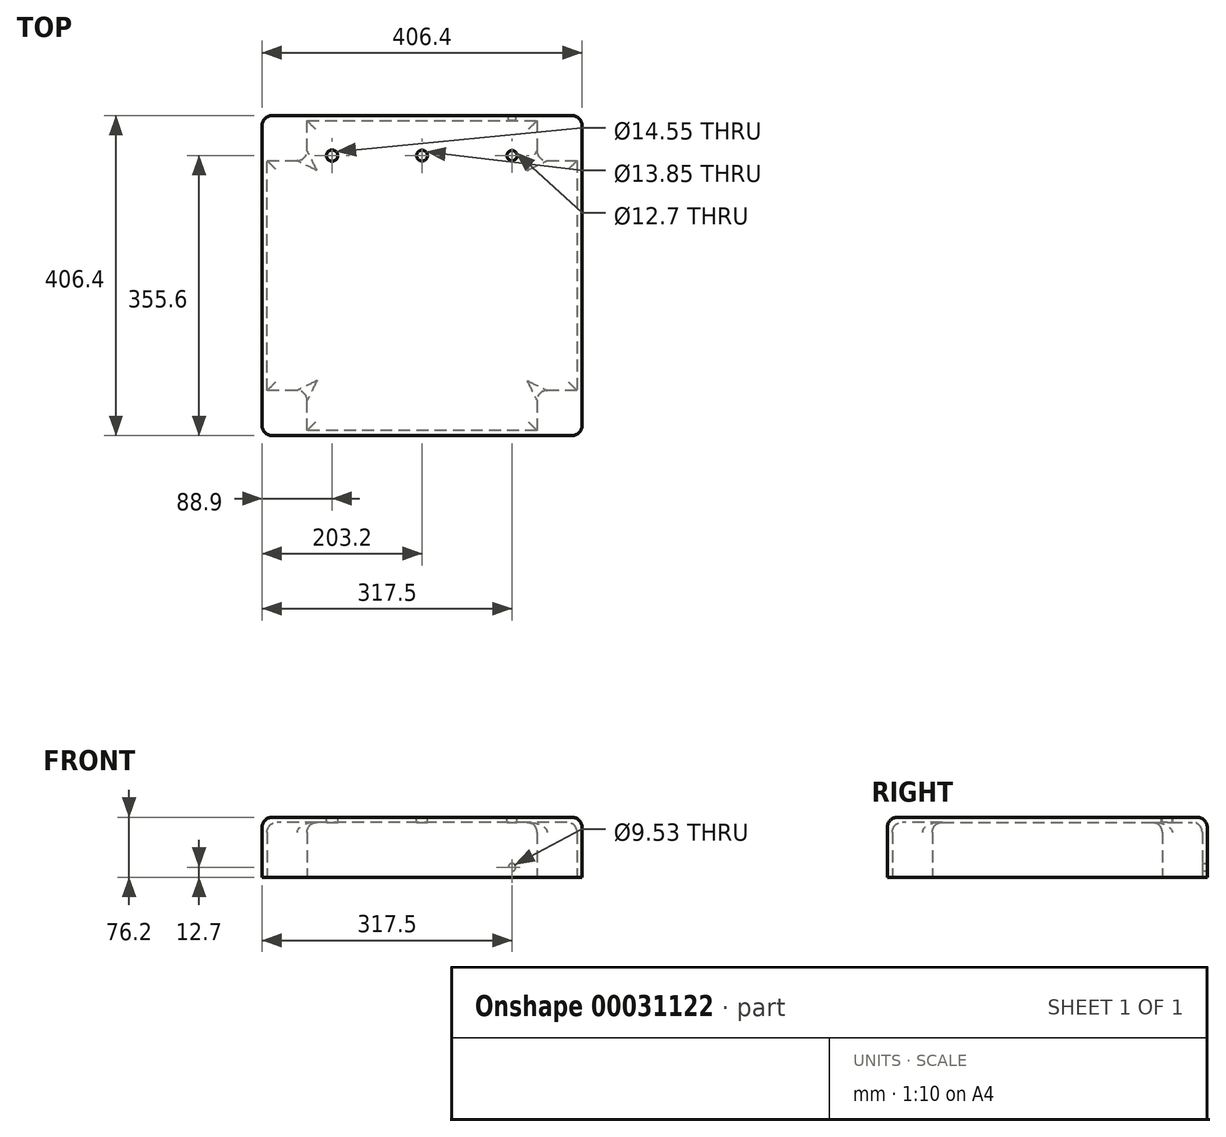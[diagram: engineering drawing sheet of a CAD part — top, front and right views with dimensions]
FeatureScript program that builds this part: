
annotation { "Feature Type Name" : "Feature", "Feature Type Description" : "" }
export const myFeature = defineFeature(function(context is Context, id is Id, definition is map)
    precondition{}
    {
        {
            var Q0;
            Q0=qCreatedBy(makeId("Top.planeOp"),FACE);
            var sketch = newSketch(context, id + "F0", { "sketchPlane" : qUnion([Q0])});
            skLineSegment(sketch, "E0.bottom", {"start": v(-203.2, 203.2) * mm, "end": v(203.2, 203.2) * mm});
            skLineSegment(sketch, "E0.top", {"start": v(-203.2, -203.2) * mm, "end": v(203.2, -203.2) * mm});
            skLineSegment(sketch, "E0.left", {"start": v(-203.2, 203.2) * mm, "end": v(-203.2, -203.2) * mm});
            skLineSegment(sketch, "E0.right", {"start": v(203.2, 203.2) * mm, "end": v(203.2, -203.2) * mm});
            skSolve(sketch);
        }
        {
            var Q0;
            Q0=makeQuery(id+"F0.imprint","IMPRINT",FACE,{"disambiguationData":[TD([[makeQuery(id+"F0.imprint","IMPRINT",EDGE,{"derivedFrom":sQuery(id+"F0.wireOp",EDGE,"E0.bottom")}),-1.0]])]});
            extrude(context, id + "F1", {"entities" : qUnion([Q0]), "depth" : 76.2 * mm});
        }
        {
            var Q0;
            Q0=makeQuery(id+"F1.opExtrude","SWEPT_EDGE",EDGE,{"disambiguationData":[OSD([sQuery(id+"F0.wireOp",EDGE,"E0.top"),sQuery(id+"F0.wireOp",EDGE,"E0.right")])]});
            var Q1;
            Q1=makeQuery(id+"F1.opExtrude","SWEPT_EDGE",EDGE,{"disambiguationData":[OSD([sQuery(id+"F0.wireOp",EDGE,"E0.bottom"),sQuery(id+"F0.wireOp",EDGE,"E0.right")])]});
            var Q2;
            Q2=makeQuery(id+"F1.opExtrude","SWEPT_EDGE",EDGE,{"disambiguationData":[OSD([sQuery(id+"F0.wireOp",EDGE,"E0.top"),sQuery(id+"F0.wireOp",EDGE,"E0.left")])]});
            var Q3;
            Q3=makeQuery(id+"F1.opExtrude","SWEPT_EDGE",EDGE,{"disambiguationData":[OSD([sQuery(id+"F0.wireOp",EDGE,"E0.bottom"),sQuery(id+"F0.wireOp",EDGE,"E0.left")])]});
            fillet(context, id + "F2", {"entities" : qUnion([Q0, Q1, Q2, Q3]), "radius" : 12.7 * mm, "tangentPropagation" : true, "allowEdgeOverflow" : false});
        }
        {
            var Q0;
            Q0=makeQuery(id+"F1.opExtrude","CAP_FACE",FACE,{"disambiguationData":[OSD([sQuery(id+"F0.wireOp",EDGE,"E0.bottom"),sQuery(id+"F0.wireOp",EDGE,"E0.top"),sQuery(id+"F0.wireOp",EDGE,"E0.left"),sQuery(id+"F0.wireOp",EDGE,"E0.right")])],"isStart":true});
            var sketch = newSketch(context, id + "F3", { "sketchPlane" : qUnion([Q0])});
            skLineSegment(sketch, "E1", {"start": v(-146.05, 196.85) * mm, "end": v(-146.05, 146.05) * mm});
            skLineSegment(sketch, "E2", {"start": v(-146.05, 146.05) * mm, "end": v(-196.85, 146.05) * mm});
            skLineSegment(sketch, "E3", {"start": v(-196.85, 146.05) * mm, "end": v(-196.85, -146.05) * mm});
            skLineSegment(sketch, "E4", {"start": v(-196.85, -146.05) * mm, "end": v(-146.05, -146.05) * mm});
            skLineSegment(sketch, "E5", {"start": v(-146.05, -146.05) * mm, "end": v(-146.05, -196.85) * mm});
            skLineSegment(sketch, "E6", {"start": v(-146.05, -196.85) * mm, "end": v(146.05, -196.85) * mm});
            skLineSegment(sketch, "E7", {"start": v(146.05, -196.85) * mm, "end": v(146.05, -146.05) * mm});
            skLineSegment(sketch, "E8", {"start": v(146.05, -146.05) * mm, "end": v(196.85, -146.05) * mm});
            skLineSegment(sketch, "E9", {"start": v(196.85, -146.05) * mm, "end": v(196.85, 146.05) * mm});
            skLineSegment(sketch, "E10", {"start": v(196.85, 146.05) * mm, "end": v(146.05, 146.05) * mm});
            skLineSegment(sketch, "E11", {"start": v(146.05, 146.05) * mm, "end": v(146.05, 196.85) * mm});
            skLineSegment(sketch, "E12", {"start": v(146.05, 196.85) * mm, "end": v(-146.05, 196.85) * mm});
            skSolve(sketch);
        }
        {
            var Q0;
            Q0=makeQuery(id+"F3.imprint","IMPRINT",FACE,{"disambiguationData":[TD([[makeQuery(id+"F3.imprint","IMPRINT",EDGE,{"derivedFrom":sQuery(id+"F3.wireOp",EDGE,"E1")}),1.0]])]});
            extrude(context, id + "F4", {"entities" : qUnion([Q0]), "operationType" : NewBodyOperationType.REMOVE, "oppositeDirection" : true, "depth" : 69.85 * mm});
        }
        {
            var Q0;
            Q0=makeQuery(id+"F4.boolean.opBoolean","COPY",EDGE,{"derivedFrom":makeQuery(id+"F4.opExtrude","CAP_EDGE",EDGE,{"disambiguationData":[OSD([sQuery(id+"F3.wireOp",EDGE,"E12")])],"isStart":false})});
            var Q1;
            Q1=makeQuery(id+"F4.boolean.opBoolean","COPY",EDGE,{"derivedFrom":makeQuery(id+"F4.opExtrude","CAP_EDGE",EDGE,{"disambiguationData":[OSD([sQuery(id+"F3.wireOp",EDGE,"E1")])],"isStart":false})});
            var Q2;
            Q2=makeQuery(id+"F4.boolean.opBoolean","COPY",EDGE,{"derivedFrom":makeQuery(id+"F4.opExtrude","CAP_EDGE",EDGE,{"disambiguationData":[OSD([sQuery(id+"F3.wireOp",EDGE,"E2")])],"isStart":false})});
            var Q3;
            Q3=makeQuery(id+"F4.boolean.opBoolean","COPY",EDGE,{"derivedFrom":makeQuery(id+"F4.opExtrude","CAP_EDGE",EDGE,{"disambiguationData":[OSD([sQuery(id+"F3.wireOp",EDGE,"E3")])],"isStart":false})});
            var Q4;
            Q4=makeQuery(id+"F4.boolean.opBoolean","COPY",EDGE,{"derivedFrom":makeQuery(id+"F4.opExtrude","CAP_EDGE",EDGE,{"disambiguationData":[OSD([sQuery(id+"F3.wireOp",EDGE,"E4")])],"isStart":false})});
            var Q5;
            Q5=makeQuery(id+"F4.boolean.opBoolean","COPY",EDGE,{"derivedFrom":makeQuery(id+"F4.opExtrude","CAP_EDGE",EDGE,{"disambiguationData":[OSD([sQuery(id+"F3.wireOp",EDGE,"E5")])],"isStart":false})});
            var Q6;
            Q6=makeQuery(id+"F4.boolean.opBoolean","COPY",EDGE,{"derivedFrom":makeQuery(id+"F4.opExtrude","CAP_EDGE",EDGE,{"disambiguationData":[OSD([sQuery(id+"F3.wireOp",EDGE,"E6")])],"isStart":false})});
            var Q7;
            Q7=makeQuery(id+"F4.boolean.opBoolean","COPY",EDGE,{"derivedFrom":makeQuery(id+"F4.opExtrude","CAP_EDGE",EDGE,{"disambiguationData":[OSD([sQuery(id+"F3.wireOp",EDGE,"E7")])],"isStart":false})});
            var Q8;
            Q8=makeQuery(id+"F4.boolean.opBoolean","COPY",EDGE,{"derivedFrom":makeQuery(id+"F4.opExtrude","CAP_EDGE",EDGE,{"disambiguationData":[OSD([sQuery(id+"F3.wireOp",EDGE,"E8")])],"isStart":false})});
            var Q9;
            Q9=makeQuery(id+"F4.boolean.opBoolean","COPY",EDGE,{"derivedFrom":makeQuery(id+"F4.opExtrude","CAP_EDGE",EDGE,{"disambiguationData":[OSD([sQuery(id+"F3.wireOp",EDGE,"E9")])],"isStart":false})});
            var Q10;
            Q10=makeQuery(id+"F4.boolean.opBoolean","COPY",FACE,{"derivedFrom":makeQuery(id+"F4.opExtrude","CAP_FACE",FACE,{"disambiguationData":[OSD([sQuery(id+"F3.wireOp",EDGE,"E1"),sQuery(id+"F3.wireOp",EDGE,"E2"),sQuery(id+"F3.wireOp",EDGE,"E3"),sQuery(id+"F3.wireOp",EDGE,"E4"),sQuery(id+"F3.wireOp",EDGE,"E5"),sQuery(id+"F3.wireOp",EDGE,"E6"),sQuery(id+"F3.wireOp",EDGE,"E7"),sQuery(id+"F3.wireOp",EDGE,"E8"),sQuery(id+"F3.wireOp",EDGE,"E9"),sQuery(id+"F3.wireOp",EDGE,"E10"),sQuery(id+"F3.wireOp",EDGE,"E11"),sQuery(id+"F3.wireOp",EDGE,"E12")])],"isStart":false})});
            var Q11;
            Q11=makeQuery(id+"F1.opExtrude","CAP_FACE",FACE,{"disambiguationData":[OSD([sQuery(id+"F0.wireOp",EDGE,"E0.bottom"),sQuery(id+"F0.wireOp",EDGE,"E0.top"),sQuery(id+"F0.wireOp",EDGE,"E0.left"),sQuery(id+"F0.wireOp",EDGE,"E0.right")])],"isStart":false});
            fillet(context, id + "F5", {"entities" : qUnion([Q0, Q1, Q2, Q3, Q4, Q5, Q6, Q7, Q8, Q9, Q10, Q11]), "radius" : 12.7 * mm, "tangentPropagation" : true, "allowEdgeOverflow" : false});
        }
        {
            var Q0;
            Q0=makeQuery(id+"F5.opFillet","BLEND_EDGE",EDGE,{"blendedFrom":[makeQuery(id+"F4.boolean.opBoolean","COPY",EDGE,{"derivedFrom":makeQuery(id+"F4.opExtrude","CAP_EDGE",EDGE,{"disambiguationData":[OSD([sQuery(id+"F3.wireOp",EDGE,"E7")])],"isStart":false})}),makeQuery(id+"F4.boolean.opBoolean","COPY",EDGE,{"derivedFrom":makeQuery(id+"F4.opExtrude","CAP_EDGE",EDGE,{"disambiguationData":[OSD([sQuery(id+"F3.wireOp",EDGE,"E8")])],"isStart":false})})],"blendedInto":[]});
            var Q1;
            Q1=makeQuery(id+"F4.boolean.opBoolean","COPY",EDGE,{"derivedFrom":makeQuery(id+"F4.opExtrude","SWEPT_EDGE",EDGE,{"disambiguationData":[OSD([sQuery(id+"F3.wireOp",EDGE,"E10"),sQuery(id+"F3.wireOp",EDGE,"E11")])]})});
            var Q2;
            Q2=makeQuery(id+"F4.boolean.opBoolean","COPY",EDGE,{"derivedFrom":makeQuery(id+"F4.opExtrude","SWEPT_EDGE",EDGE,{"disambiguationData":[OSD([sQuery(id+"F3.wireOp",EDGE,"E1"),sQuery(id+"F3.wireOp",EDGE,"E2")])]})});
            var Q3;
            Q3=makeQuery(id+"F4.boolean.opBoolean","COPY",EDGE,{"derivedFrom":makeQuery(id+"F4.opExtrude","SWEPT_EDGE",EDGE,{"disambiguationData":[OSD([sQuery(id+"F3.wireOp",EDGE,"E4"),sQuery(id+"F3.wireOp",EDGE,"E5")])]})});
            fillet(context, id + "F6", {"entities" : qUnion([Q0, Q1, Q2, Q3]), "radius" : 12.7 * mm, "tangentPropagation" : true, "allowEdgeOverflow" : false});
        }
        {
            var Q0;
            Q0=makeQuery(id+"F1.opExtrude","SWEPT_FACE",FACE,{"disambiguationData":[OSD([sQuery(id+"F0.wireOp",EDGE,"E0.bottom")])]});
            var sketch = newSketch(context, id + "F7", { "sketchPlane" : qUnion([Q0])});
            skCircle(sketch, "E13", {"center": v(-114.3, 12.7) * mm, "radius": 4.76 * mm});
            skSolve(sketch);
        }
        {
            var Q0;
            Q0=makeQuery(id+"F7.imprint","IMPRINT",FACE,{"disambiguationData":[TD([[makeQuery(id+"F7.imprint","IMPRINT",EDGE,{"derivedFrom":sQuery(id+"F7.wireOp",EDGE,"E13")}),1.0]])]});
            var Q1;
            Q1=sQuery(id+"F7.wireOp",EDGE,"E13");
            extrude(context, id + "F8", {"entities" : qUnion([Q0]), "operationType" : NewBodyOperationType.REMOVE, "surfaceEntities" : qUnion([Q1]), "oppositeDirection" : true, "depth" : 25.4 * mm});
        }
        {
            var Q0;
            Q0=makeQuery(id+"F1.opExtrude","CAP_FACE",FACE,{"disambiguationData":[OSD([sQuery(id+"F0.wireOp",EDGE,"E0.bottom"),sQuery(id+"F0.wireOp",EDGE,"E0.top"),sQuery(id+"F0.wireOp",EDGE,"E0.left"),sQuery(id+"F0.wireOp",EDGE,"E0.right")])],"isStart":false});
            var sketch = newSketch(context, id + "F9", { "sketchPlane" : qUnion([Q0])});
            skCircle(sketch, "E14", {"center": v(114.3, 152.4) * mm, "radius": 6.35 * mm});
            skCircle(sketch, "E15", {"center": v(0, 152.4) * mm, "radius": 6.93 * mm});
            skCircle(sketch, "E16", {"center": v(-114.3, 152.4) * mm, "radius": 7.27 * mm});
            skSolve(sketch);
        }
        {
            var Q0;
            Q0 = qSketchRegion(id + "F9", true);
            extrude(context, id + "F10", {"entities" : qUnion([Q0]), "operationType" : NewBodyOperationType.REMOVE, "oppositeDirection" : true, "depth" : 25.4 * mm});
        }
    });
